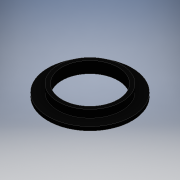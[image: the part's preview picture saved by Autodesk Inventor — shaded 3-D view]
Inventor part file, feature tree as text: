
AUTODESK INVENTOR PART (.ipt)
format: ipt  version: 2020.2 (Build 242310000, 310)  size: 105,984 bytes
history: native  units: mm
features: extrude x2, other x1, sketch x1
ambient origin geometry x8: Origin, YZ Plane, XZ Plane, XY Plane, X Axis, Y Axis, Z Axis, Center Point
bodies: Body1 (feature_tree)
feature tree (4):
  other  "ソリッド1"
  sketch  "スケッチ1"
  extrude  "押し出し1"  Depth=22.0mm
  extrude  "押し出し2"  Depth=25.0mm
